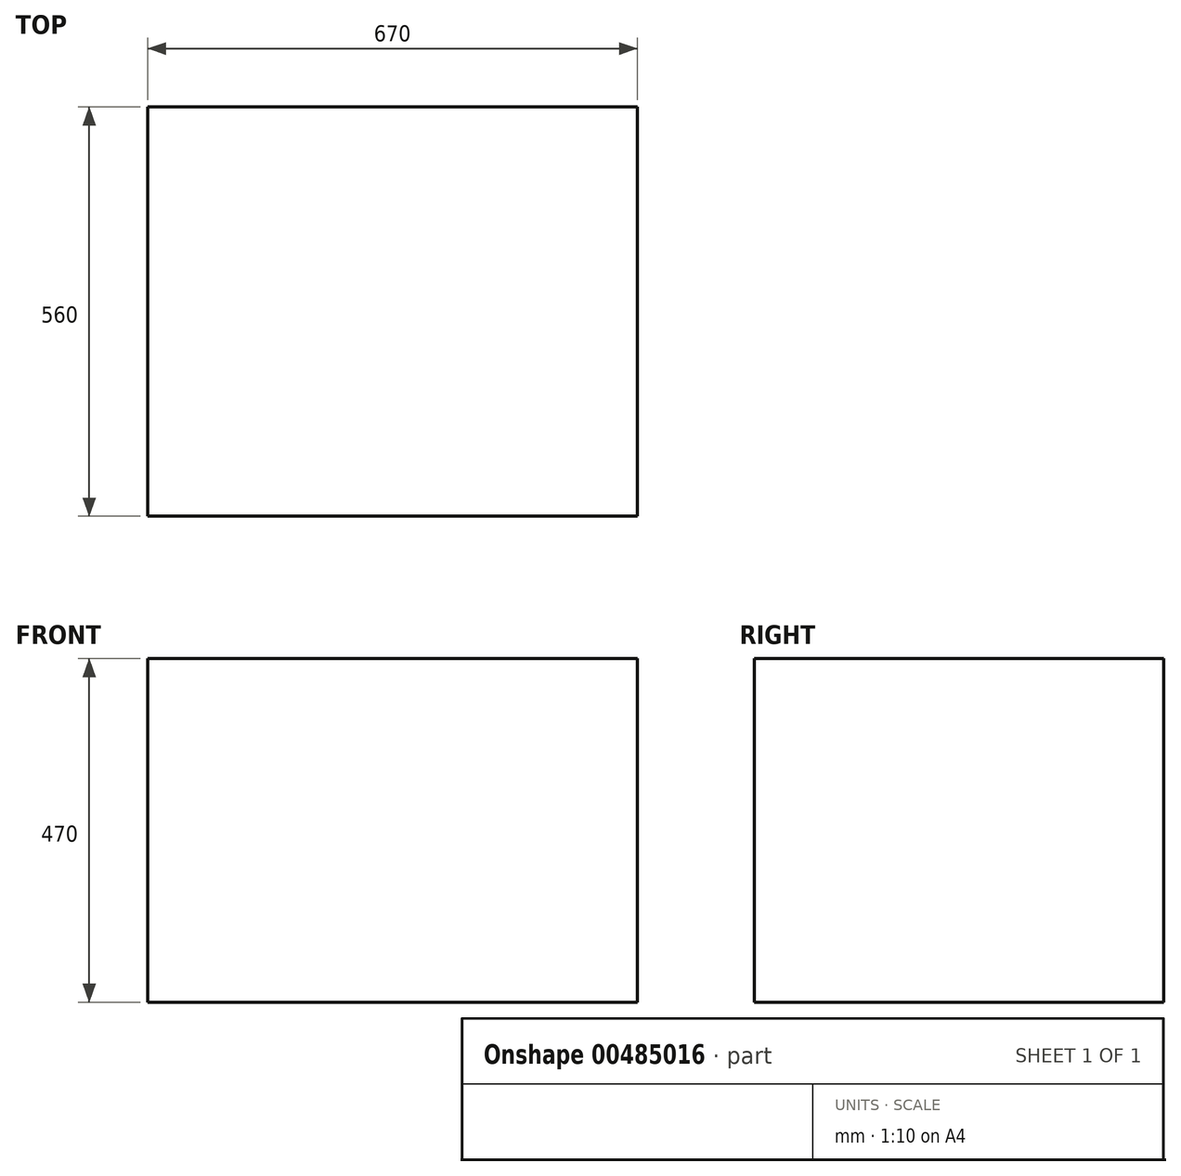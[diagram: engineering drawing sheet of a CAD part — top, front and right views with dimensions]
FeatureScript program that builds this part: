
annotation { "Feature Type Name" : "Feature", "Feature Type Description" : "" }
export const myFeature = defineFeature(function(context is Context, id is Id, definition is map)
    precondition{}
    {
        {
            var Q0;
            Q0=qCreatedBy(makeId("Top.planeOp"),FACE);
            var sketch = newSketch(context, id + "F0", { "sketchPlane" : qUnion([Q0])});
            skLineSegment(sketch, "E0.bottom", {"start": v(335, 280) * mm, "end": v(-335, 280) * mm});
            skLineSegment(sketch, "E0.top", {"start": v(335, -280) * mm, "end": v(-335, -280) * mm});
            skLineSegment(sketch, "E0.left", {"start": v(335, 280) * mm, "end": v(335, -280) * mm});
            skLineSegment(sketch, "E0.right", {"start": v(-335, 280) * mm, "end": v(-335, -280) * mm});
            skPoint(sketch, "E0.middle", {"position": v(0, 0) * mm});
            skSolve(sketch);
        }
        {
            var Q0;
            Q0=makeQuery(id+"F0.imprint","IMPRINT",FACE,{"disambiguationData":[TD([[makeQuery(id+"F0.imprint","IMPRINT",EDGE,{"derivedFrom":sQuery(id+"F0.wireOp",EDGE,"E0.bottom")}),1.0]])]});
            extrude(context, id + "F1", {"entities" : qUnion([Q0]), "depth" : 470 * mm, "offsetDistance" : 25 * mm});
        }
    });
